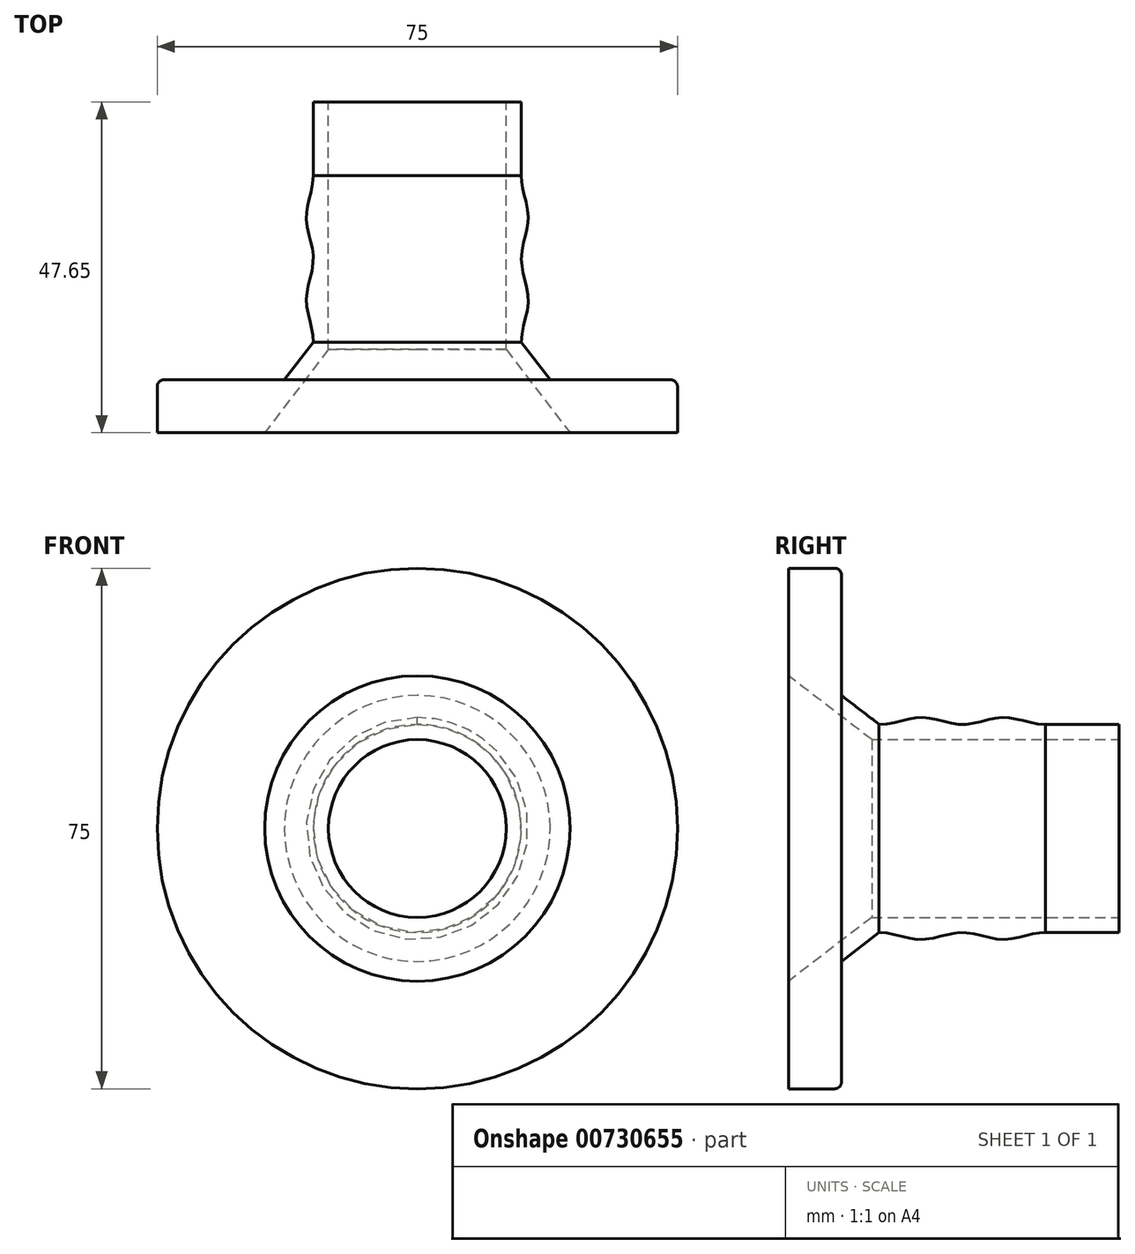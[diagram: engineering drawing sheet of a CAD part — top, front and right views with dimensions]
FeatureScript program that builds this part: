
annotation { "Feature Type Name" : "Feature", "Feature Type Description" : "" }
export const myFeature = defineFeature(function(context is Context, id is Id, definition is map)
    precondition{}
    {
        {
            var Q0;
            Q0=qCreatedBy(makeId("Top.planeOp"),FACE);
            var sketch = newSketch(context, id + "F0", { "sketchPlane" : qUnion([Q0])});
            skLineSegment(sketch, "E0", {"start": v(0, 53.9) * mm, "end": v(0, -40.69) * mm, "construction": true});
            skLineSegment(sketch, "E1", {"start": v(-22, 0) * mm, "end": v(-37.5, 0) * mm});
            skLineSegment(sketch, "E2", {"start": v(-37.5, 0) * mm, "end": v(-37.5, 7.65) * mm});
            skLineSegment(sketch, "E3", {"start": v(-37.5, 7.65) * mm, "end": v(-19.16, 7.65) * mm});
            skLineSegment(sketch, "E4", {"start": v(-24, 7.65) * mm, "end": v(-24, 53.8) * mm, "construction": true});
            skLineSegment(sketch, "E5", {"start": v(-15, 37.08) * mm, "end": v(-15, 47.65) * mm});
            skLineSegment(sketch, "E6", {"start": v(-15, 47.65) * mm, "end": v(-15, 47.65) * mm});
            skLineSegment(sketch, "E7", {"start": v(-15, 47.65) * mm, "end": v(-12.8, 47.65) * mm});
            skLineSegment(sketch, "E8", {"start": v(-12.8, 47.65) * mm, "end": v(-12.8, 12) * mm});
            skLineSegment(sketch, "E9", {"start": v(-22, 0) * mm, "end": v(-12.8, 12) * mm});
            skLineSegment(sketch, "E10", {"start": v(-19.16, 7.65) * mm, "end": v(-15, 13.08) * mm});
            skLineSegment(sketch, "E11", {"start": v(-16, 53.39) * mm, "end": v(-16, -9.24) * mm, "construction": true});
            skFitSpline(sketch, "E12", {"points": [v(-15, 13.08) * mm, v(-16, 19.08) * mm, v(-15, 25.08) * mm, v(-16, 31.08) * mm, v(-15, 37.08) * mm], "startDerivative": vector(0.13, 26.42) * mm, "endDerivative": vector(0, 27.99) * mm});
            skSolve(sketch);
        }
        {
            var Q0;
            Q0=qSketchRegion(id+"F0",true);
            var Q1;
            Q1=sQuery(id+"F0.wireOp",EDGE,"E0");
            revolve(context, id + "F1", {"surfaceOperationType" : NewSurfaceOperationType.NEW, "entities" : qUnion([Q0]), "axis" : qUnion([Q1]), "revolveType" : RevolveType.FULL});
        }
        {
            var Q0;
            Q0=makeQuery(id+"F1.opRevolve","SWEPT_EDGE",EDGE,{"disambiguationData":[OSD([sQuery(id+"F0.wireOp",EDGE,"E2"),sQuery(id+"F0.wireOp",EDGE,"E3")])]});
            fillet(context, id + "F2", {"entities" : qUnion([Q0]), "radius" : 1 * mm, "tangentPropagation" : true, "allowEdgeOverflow" : false});
        }
    });
